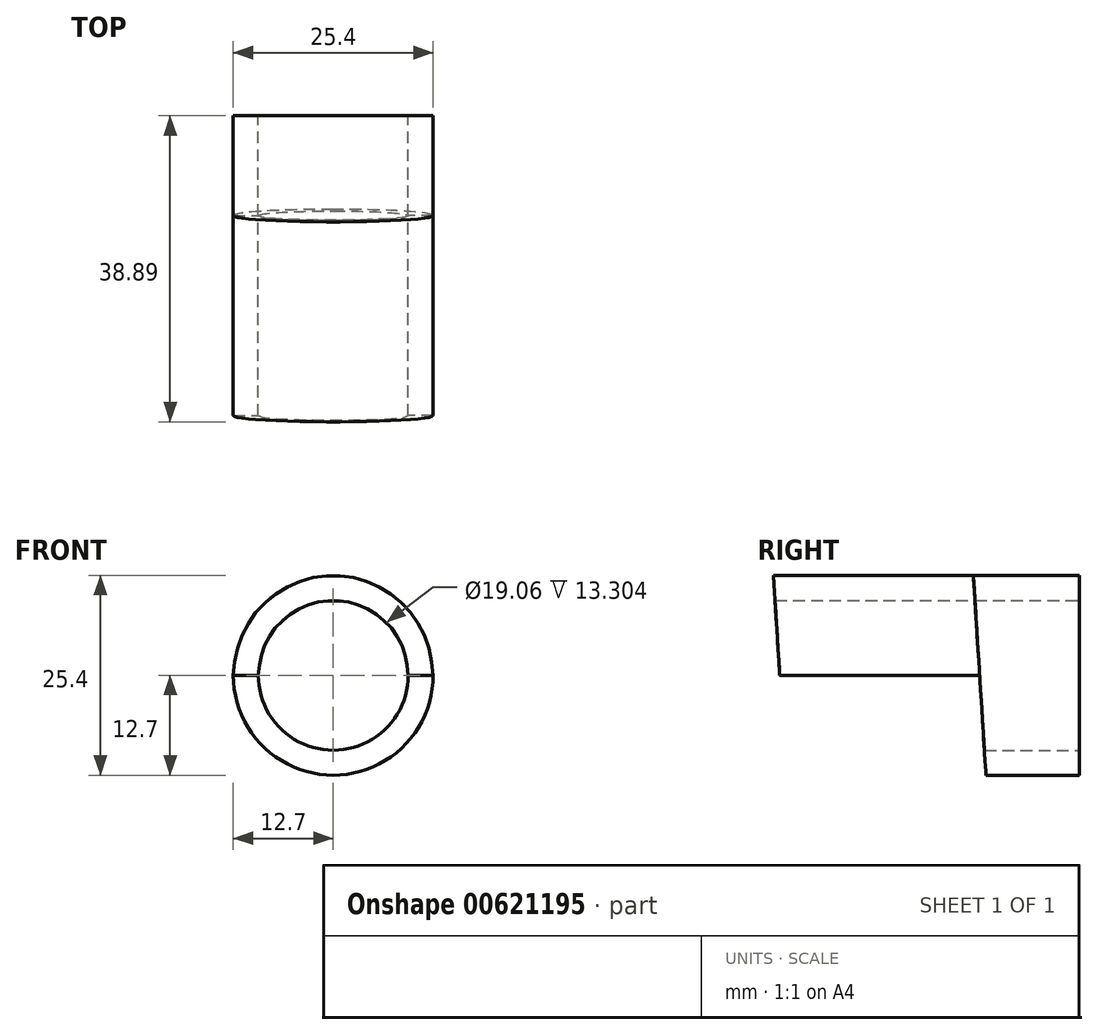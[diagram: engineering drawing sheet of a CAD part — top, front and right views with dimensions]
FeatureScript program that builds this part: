
annotation { "Feature Type Name" : "Feature", "Feature Type Description" : "" }
export const myFeature = defineFeature(function(context is Context, id is Id, definition is map)
    precondition{}
    {
        {
            var Q0;
            Q0=qCreatedBy(makeId("Front.planeOp"),FACE);
            var sketch = newSketch(context, id + "F0", { "sketchPlane" : qUnion([Q0])});
            skCircle(sketch, "E0", {"center": v(0, 0) * mm, "radius": 9.53 * mm});
            skCircle(sketch, "E1", {"center": v(0, 0) * mm, "radius": 12.7 * mm});
            skSolve(sketch);
        }
        {
            var Q0;
            Q0=makeQuery(id+"F0.imprint","IMPRINT",FACE,{"disambiguationData":[TD([[makeQuery(id+"F0.imprint","IMPRINT",EDGE,{"derivedFrom":sQuery(id+"F0.wireOp",EDGE,"6qHw69TV-ns71-QR00-segl-mkystgBmmhuX")}),-1.0]])]});
            var Q1;
            Q1=makeQuery(id+"F0.imprint","IMPRINT",FACE,{"disambiguationData":[TD([[makeQuery(id+"F0.imprint","IMPRINT",EDGE,{"derivedFrom":sQuery(id+"F0.wireOp",EDGE,"E0")}),-1.0]])]});
            var Q2;
            Q2=makeQuery(id+"F0.imprint","IMPRINT",FACE,{"disambiguationData":[TD([[makeQuery(id+"F0.imprint","IMPRINT",EDGE,{"derivedFrom":sQuery(id+"F0.wireOp",EDGE,"VdreAass-U2ki-OOkh-u9lk-LOK2N8HoCZDs")}),-1.0]])]});
            extrude(context, id + "F1", {"entities" : qUnion([Q0, Q1, Q2]), "depth" : 50.8 * mm, "offsetDistance" : 25.4 * mm});
        }
        {
            var Q0;
            Q0=qCreatedBy(makeId("Right.planeOp"),FACE);
            var sketch = newSketch(context, id + "F2", { "sketchPlane" : qUnion([Q0])});
            skLineSegment(sketch, "E2", {"start": v(0, 0) * mm, "end": v(0, 50.8) * mm});
            skLineSegment(sketch, "E3", {"start": v(0, 50.8) * mm, "end": v(-41.28, 50.8) * mm});
            skLineSegment(sketch, "E4", {"start": v(0, 0) * mm, "end": v(-38.1, 0) * mm});
            skLineSegment(sketch, "E5", {"start": v(-38.1, 0) * mm, "end": v(-41.27, 50.8) * mm});
            skLineSegment(sketch, "E6", {"start": v(-41.27, 50.8) * mm, "end": v(-42.5, 70.4) * mm});
            skLineSegment(sketch, "E7", {"start": v(-42.5, 70.4) * mm, "end": v(0, 70.4) * mm});
            skLineSegment(sketch, "E8", {"start": v(0, 70.4) * mm, "end": v(0, 50.8) * mm});
            skLineSegment(sketch, "E9", {"start": v(-38.1, 0) * mm, "end": v(-36.66, -22.97) * mm});
            skLineSegment(sketch, "E10", {"start": v(-36.66, -22.97) * mm, "end": v(0, -22.97) * mm});
            skLineSegment(sketch, "E11", {"start": v(0, -22.97) * mm, "end": v(0, 0) * mm});
            skLineSegment(sketch, "E12", {"start": v(-42.5, 70.4) * mm, "end": v(-59.35, 70.4) * mm});
            skLineSegment(sketch, "E13", {"start": v(-59.35, 70.4) * mm, "end": v(-59.35, -22.97) * mm});
            skLineSegment(sketch, "E14", {"start": v(-59.35, -22.97) * mm, "end": v(-36.66, -22.97) * mm});
            skLineSegment(sketch, "E15", {"start": v(0, 0) * mm, "end": v(-12.7, 0) * mm});
            skLineSegment(sketch, "E16", {"start": v(-12.7, 0) * mm, "end": v(-15.88, 50.8) * mm});
            skLineSegment(sketch, "E17", {"start": v(-15.88, 50.8) * mm, "end": v(-11.26, -22.97) * mm});
            skSolve(sketch);
        }
        {
            var Q0;
            Q0=makeQuery(id+"F2.imprint","IMPRINT",FACE,{"disambiguationData":[TD([[makeQuery(id+"F2.imprint","IMPRINT",EDGE,{"derivedFrom":sQuery(id+"F2.wireOp",EDGE,"E5")}),1.0]])]});
            var Q1;
            {var subQ4=sQuery(id+"F2.wireOp",EDGE,"E4");Q1=makeQuery(id+"F2.imprint","IMPRINT",FACE,{"disambiguationData":[TD([[makeQuery(id+"F2.imprint","IMPRINT",EDGE,{"derivedFrom":subQ4}),-1.0]])]});}
            var Q2;
            {var subQ0=sQuery(id+"F2.wireOp",EDGE,"E4");Q2=makeQuery(id+"F2.imprint","IMPRINT",FACE,{"disambiguationData":[TD([[makeQuery(id+"F2.imprint","IMPRINT",EDGE,{"derivedFrom":subQ0}),1.0]])]});}
            extrude(context, id + "F3", {"entities" : qUnion([Q0, Q1, Q2]), "operationType" : NewBodyOperationType.REMOVE, "oppositeDirection" : true, "depth" : 25.4 * mm, "offsetDistance" : 25.4 * mm});
        }
        {
            var Q0;
            Q0=makeQuery(id+"F2.imprint","IMPRINT",FACE,{"disambiguationData":[TD([[makeQuery(id+"F2.imprint","IMPRINT",EDGE,{"derivedFrom":sQuery(id+"F2.wireOp",EDGE,"E5")}),1.0]])]});
            var Q1;
            {var subQ4=sQuery(id+"F2.wireOp",EDGE,"E4");Q1=makeQuery(id+"F2.imprint","IMPRINT",FACE,{"disambiguationData":[TD([[makeQuery(id+"F2.imprint","IMPRINT",EDGE,{"derivedFrom":subQ4}),-1.0]])]});}
            var Q2;
            {var subQ0=sQuery(id+"F2.wireOp",EDGE,"E4");Q2=makeQuery(id+"F2.imprint","IMPRINT",FACE,{"disambiguationData":[TD([[makeQuery(id+"F2.imprint","IMPRINT",EDGE,{"derivedFrom":subQ0}),1.0]])]});}
            extrude(context, id + "F4", {"entities" : qUnion([Q0, Q1, Q2]), "operationType" : NewBodyOperationType.REMOVE, "depth" : 25.4 * mm, "offsetDistance" : 25.4 * mm});
        }
    });
